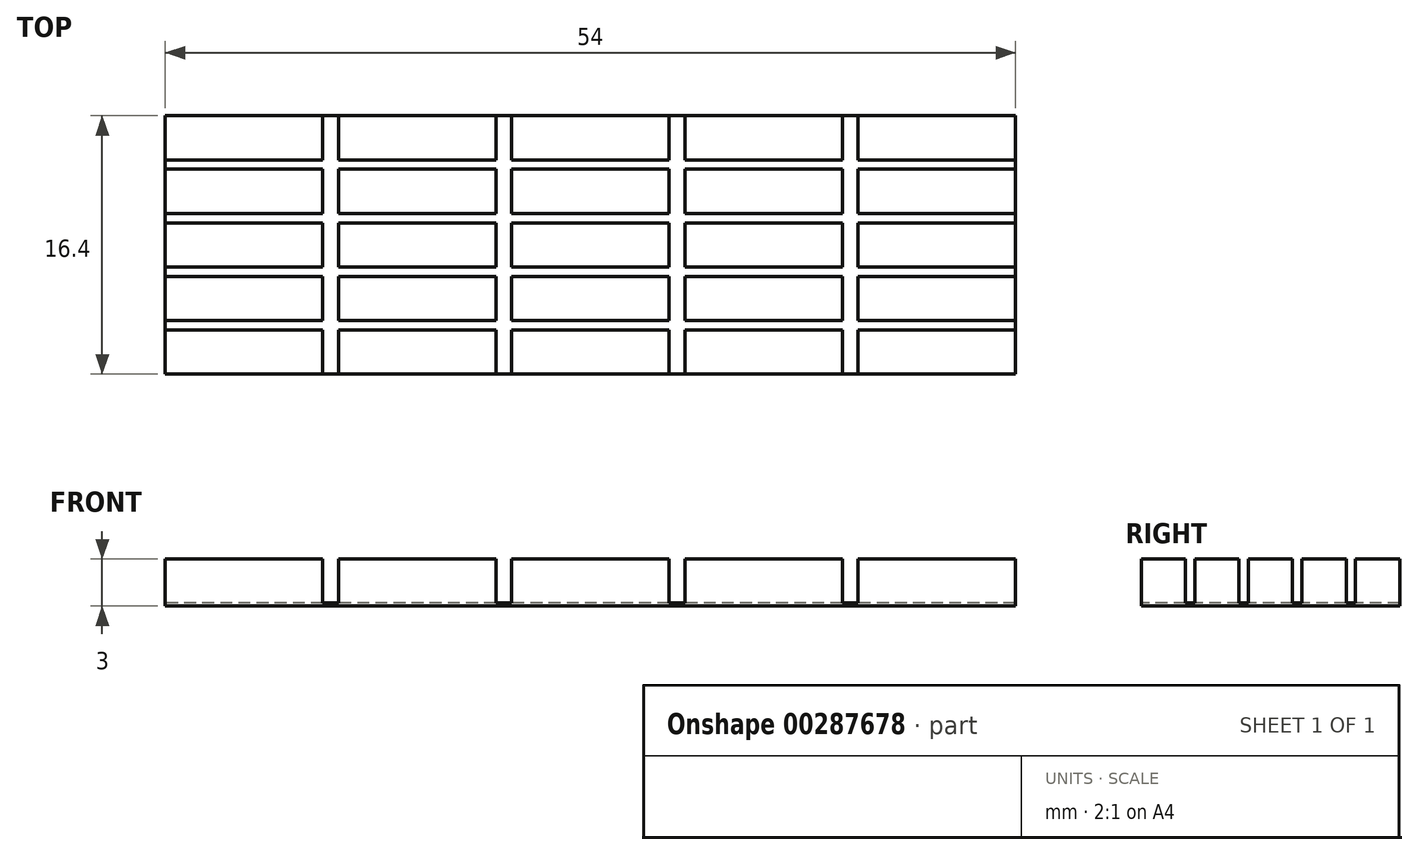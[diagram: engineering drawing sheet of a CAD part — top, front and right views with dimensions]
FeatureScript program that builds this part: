
annotation { "Feature Type Name" : "Feature", "Feature Type Description" : "" }
export const myFeature = defineFeature(function(context is Context, id is Id, definition is map)
    precondition{}
    {
        {
            var Q0;
            Q0=qCreatedBy(makeId("Top.planeOp"),FACE);
            var sketch = newSketch(context, id + "F0", { "sketchPlane" : qUnion([Q0])});
            skLineSegment(sketch, "E0", {"start": v(0, 0) * mm, "end": v(33.88, 0) * mm, "construction": true});
            skLineSegment(sketch, "E1", {"start": v(0, 0) * mm, "end": v(0, 25.36) * mm, "construction": true});
            skLineSegment(sketch, "E2.bottom", {"start": v(0, 0) * mm, "end": v(10, 0) * mm});
            skLineSegment(sketch, "E2.top", {"start": v(0, 2.8) * mm, "end": v(10, 2.8) * mm});
            skLineSegment(sketch, "E2.left", {"start": v(0, 0) * mm, "end": v(0, 2.8) * mm});
            skLineSegment(sketch, "E2.right", {"start": v(10, 0) * mm, "end": v(10, 2.8) * mm});
            skLineSegment(sketch, "E3.0.1.0", {"start": v(0, 6.2) * mm, "end": v(10, 6.2) * mm});
            skLineSegment(sketch, "E3.0.1.1", {"start": v(10, 3.4) * mm, "end": v(10, 6.2) * mm});
            skLineSegment(sketch, "E3.0.1.2", {"start": v(0, 3.4) * mm, "end": v(10, 3.4) * mm});
            skLineSegment(sketch, "E3.0.1.3", {"start": v(0, 3.4) * mm, "end": v(0, 6.2) * mm});
            skLineSegment(sketch, "E3.0.2.0", {"start": v(0, 9.6) * mm, "end": v(10, 9.6) * mm});
            skLineSegment(sketch, "E3.0.2.1", {"start": v(10, 6.8) * mm, "end": v(10, 9.6) * mm});
            skLineSegment(sketch, "E3.0.2.2", {"start": v(0, 6.8) * mm, "end": v(10, 6.8) * mm});
            skLineSegment(sketch, "E3.0.2.3", {"start": v(0, 6.8) * mm, "end": v(0, 9.6) * mm});
            skLineSegment(sketch, "E3.0.3.0", {"start": v(0, 13) * mm, "end": v(10, 13) * mm});
            skLineSegment(sketch, "E3.0.3.1", {"start": v(10, 10.2) * mm, "end": v(10, 13) * mm});
            skLineSegment(sketch, "E3.0.3.2", {"start": v(0, 10.2) * mm, "end": v(10, 10.2) * mm});
            skLineSegment(sketch, "E3.0.3.3", {"start": v(0, 10.2) * mm, "end": v(0, 13) * mm});
            skLineSegment(sketch, "E3.0.4.0", {"start": v(0, 16.4) * mm, "end": v(10, 16.4) * mm});
            skLineSegment(sketch, "E3.0.4.1", {"start": v(10, 13.6) * mm, "end": v(10, 16.4) * mm});
            skLineSegment(sketch, "E3.0.4.2", {"start": v(0, 13.6) * mm, "end": v(10, 13.6) * mm});
            skLineSegment(sketch, "E3.0.4.3", {"start": v(0, 13.6) * mm, "end": v(0, 16.4) * mm});
            skLineSegment(sketch, "E3.1.0.0", {"start": v(11, 2.8) * mm, "end": v(21, 2.8) * mm});
            skLineSegment(sketch, "E3.1.0.1", {"start": v(21, 0) * mm, "end": v(21, 2.8) * mm});
            skLineSegment(sketch, "E3.1.0.2", {"start": v(11, 0) * mm, "end": v(21, 0) * mm});
            skLineSegment(sketch, "E3.1.0.3", {"start": v(11, 0) * mm, "end": v(11, 2.8) * mm});
            skLineSegment(sketch, "E3.1.1.0", {"start": v(11, 6.2) * mm, "end": v(21, 6.2) * mm});
            skLineSegment(sketch, "E3.1.1.1", {"start": v(21, 3.4) * mm, "end": v(21, 6.2) * mm});
            skLineSegment(sketch, "E3.1.1.2", {"start": v(11, 3.4) * mm, "end": v(21, 3.4) * mm});
            skLineSegment(sketch, "E3.1.1.3", {"start": v(11, 3.4) * mm, "end": v(11, 6.2) * mm});
            skLineSegment(sketch, "E3.1.2.0", {"start": v(11, 9.6) * mm, "end": v(21, 9.6) * mm});
            skLineSegment(sketch, "E3.1.2.1", {"start": v(21, 6.8) * mm, "end": v(21, 9.6) * mm});
            skLineSegment(sketch, "E3.1.2.2", {"start": v(11, 6.8) * mm, "end": v(21, 6.8) * mm});
            skLineSegment(sketch, "E3.1.2.3", {"start": v(11, 6.8) * mm, "end": v(11, 9.6) * mm});
            skLineSegment(sketch, "E3.1.3.0", {"start": v(11, 13) * mm, "end": v(21, 13) * mm});
            skLineSegment(sketch, "E3.1.3.1", {"start": v(21, 10.2) * mm, "end": v(21, 13) * mm});
            skLineSegment(sketch, "E3.1.3.2", {"start": v(11, 10.2) * mm, "end": v(21, 10.2) * mm});
            skLineSegment(sketch, "E3.1.3.3", {"start": v(11, 10.2) * mm, "end": v(11, 13) * mm});
            skLineSegment(sketch, "E3.1.4.0", {"start": v(11, 16.4) * mm, "end": v(21, 16.4) * mm});
            skLineSegment(sketch, "E3.1.4.1", {"start": v(21, 13.6) * mm, "end": v(21, 16.4) * mm});
            skLineSegment(sketch, "E3.1.4.2", {"start": v(11, 13.6) * mm, "end": v(21, 13.6) * mm});
            skLineSegment(sketch, "E3.1.4.3", {"start": v(11, 13.6) * mm, "end": v(11, 16.4) * mm});
            skLineSegment(sketch, "E3.2.0.0", {"start": v(22, 2.8) * mm, "end": v(32, 2.8) * mm});
            skLineSegment(sketch, "E3.2.0.1", {"start": v(32, 0) * mm, "end": v(32, 2.8) * mm});
            skLineSegment(sketch, "E3.2.0.2", {"start": v(22, 0) * mm, "end": v(32, 0) * mm});
            skLineSegment(sketch, "E3.2.0.3", {"start": v(22, 0) * mm, "end": v(22, 2.8) * mm});
            skLineSegment(sketch, "E3.2.1.0", {"start": v(22, 6.2) * mm, "end": v(32, 6.2) * mm});
            skLineSegment(sketch, "E3.2.1.1", {"start": v(32, 3.4) * mm, "end": v(32, 6.2) * mm});
            skLineSegment(sketch, "E3.2.1.2", {"start": v(22, 3.4) * mm, "end": v(32, 3.4) * mm});
            skLineSegment(sketch, "E3.2.1.3", {"start": v(22, 3.4) * mm, "end": v(22, 6.2) * mm});
            skLineSegment(sketch, "E3.2.2.0", {"start": v(22, 9.6) * mm, "end": v(32, 9.6) * mm});
            skLineSegment(sketch, "E3.2.2.1", {"start": v(32, 6.8) * mm, "end": v(32, 9.6) * mm});
            skLineSegment(sketch, "E3.2.2.2", {"start": v(22, 6.8) * mm, "end": v(32, 6.8) * mm});
            skLineSegment(sketch, "E3.2.2.3", {"start": v(22, 6.8) * mm, "end": v(22, 9.6) * mm});
            skLineSegment(sketch, "E3.2.3.0", {"start": v(22, 13) * mm, "end": v(32, 13) * mm});
            skLineSegment(sketch, "E3.2.3.1", {"start": v(32, 10.2) * mm, "end": v(32, 13) * mm});
            skLineSegment(sketch, "E3.2.3.2", {"start": v(22, 10.2) * mm, "end": v(32, 10.2) * mm});
            skLineSegment(sketch, "E3.2.3.3", {"start": v(22, 10.2) * mm, "end": v(22, 13) * mm});
            skLineSegment(sketch, "E3.2.4.0", {"start": v(22, 16.4) * mm, "end": v(32, 16.4) * mm});
            skLineSegment(sketch, "E3.2.4.1", {"start": v(32, 13.6) * mm, "end": v(32, 16.4) * mm});
            skLineSegment(sketch, "E3.2.4.2", {"start": v(22, 13.6) * mm, "end": v(32, 13.6) * mm});
            skLineSegment(sketch, "E3.2.4.3", {"start": v(22, 13.6) * mm, "end": v(22, 16.4) * mm});
            skLineSegment(sketch, "E3.3.0.0", {"start": v(33, 2.8) * mm, "end": v(43, 2.8) * mm});
            skLineSegment(sketch, "E3.3.0.1", {"start": v(43, 0) * mm, "end": v(43, 2.8) * mm});
            skLineSegment(sketch, "E3.3.0.2", {"start": v(33, 0) * mm, "end": v(43, 0) * mm});
            skLineSegment(sketch, "E3.3.0.3", {"start": v(33, 0) * mm, "end": v(33, 2.8) * mm});
            skLineSegment(sketch, "E3.3.1.0", {"start": v(33, 6.2) * mm, "end": v(43, 6.2) * mm});
            skLineSegment(sketch, "E3.3.1.1", {"start": v(43, 3.4) * mm, "end": v(43, 6.2) * mm});
            skLineSegment(sketch, "E3.3.1.2", {"start": v(33, 3.4) * mm, "end": v(43, 3.4) * mm});
            skLineSegment(sketch, "E3.3.1.3", {"start": v(33, 3.4) * mm, "end": v(33, 6.2) * mm});
            skLineSegment(sketch, "E3.3.2.0", {"start": v(33, 9.6) * mm, "end": v(43, 9.6) * mm});
            skLineSegment(sketch, "E3.3.2.1", {"start": v(43, 6.8) * mm, "end": v(43, 9.6) * mm});
            skLineSegment(sketch, "E3.3.2.2", {"start": v(33, 6.8) * mm, "end": v(43, 6.8) * mm});
            skLineSegment(sketch, "E3.3.2.3", {"start": v(33, 6.8) * mm, "end": v(33, 9.6) * mm});
            skLineSegment(sketch, "E3.3.3.0", {"start": v(33, 13) * mm, "end": v(43, 13) * mm});
            skLineSegment(sketch, "E3.3.3.1", {"start": v(43, 10.2) * mm, "end": v(43, 13) * mm});
            skLineSegment(sketch, "E3.3.3.2", {"start": v(33, 10.2) * mm, "end": v(43, 10.2) * mm});
            skLineSegment(sketch, "E3.3.3.3", {"start": v(33, 10.2) * mm, "end": v(33, 13) * mm});
            skLineSegment(sketch, "E3.3.4.0", {"start": v(33, 16.4) * mm, "end": v(43, 16.4) * mm});
            skLineSegment(sketch, "E3.3.4.1", {"start": v(43, 13.6) * mm, "end": v(43, 16.4) * mm});
            skLineSegment(sketch, "E3.3.4.2", {"start": v(33, 13.6) * mm, "end": v(43, 13.6) * mm});
            skLineSegment(sketch, "E3.3.4.3", {"start": v(33, 13.6) * mm, "end": v(33, 16.4) * mm});
            skLineSegment(sketch, "E3.4.0.0", {"start": v(44, 2.8) * mm, "end": v(54, 2.8) * mm});
            skLineSegment(sketch, "E3.4.0.1", {"start": v(54, 0) * mm, "end": v(54, 2.8) * mm});
            skLineSegment(sketch, "E3.4.0.2", {"start": v(44, 0) * mm, "end": v(54, 0) * mm});
            skLineSegment(sketch, "E3.4.0.3", {"start": v(44, 0) * mm, "end": v(44, 2.8) * mm});
            skLineSegment(sketch, "E3.4.1.0", {"start": v(44, 6.2) * mm, "end": v(54, 6.2) * mm});
            skLineSegment(sketch, "E3.4.1.1", {"start": v(54, 3.4) * mm, "end": v(54, 6.2) * mm});
            skLineSegment(sketch, "E3.4.1.2", {"start": v(44, 3.4) * mm, "end": v(54, 3.4) * mm});
            skLineSegment(sketch, "E3.4.1.3", {"start": v(44, 3.4) * mm, "end": v(44, 6.2) * mm});
            skLineSegment(sketch, "E3.4.2.0", {"start": v(44, 9.6) * mm, "end": v(54, 9.6) * mm});
            skLineSegment(sketch, "E3.4.2.1", {"start": v(54, 6.8) * mm, "end": v(54, 9.6) * mm});
            skLineSegment(sketch, "E3.4.2.2", {"start": v(44, 6.8) * mm, "end": v(54, 6.8) * mm});
            skLineSegment(sketch, "E3.4.2.3", {"start": v(44, 6.8) * mm, "end": v(44, 9.6) * mm});
            skLineSegment(sketch, "E3.4.3.0", {"start": v(44, 13) * mm, "end": v(54, 13) * mm});
            skLineSegment(sketch, "E3.4.3.1", {"start": v(54, 10.2) * mm, "end": v(54, 13) * mm});
            skLineSegment(sketch, "E3.4.3.2", {"start": v(44, 10.2) * mm, "end": v(54, 10.2) * mm});
            skLineSegment(sketch, "E3.4.3.3", {"start": v(44, 10.2) * mm, "end": v(44, 13) * mm});
            skLineSegment(sketch, "E3.4.4.0", {"start": v(44, 16.4) * mm, "end": v(54, 16.4) * mm});
            skLineSegment(sketch, "E3.4.4.1", {"start": v(54, 13.6) * mm, "end": v(54, 16.4) * mm});
            skLineSegment(sketch, "E3.4.4.2", {"start": v(44, 13.6) * mm, "end": v(54, 13.6) * mm});
            skLineSegment(sketch, "E3.4.4.3", {"start": v(44, 13.6) * mm, "end": v(44, 16.4) * mm});
            skLineSegment(sketch, "E3.direction1", {"start": v(0, 2.8) * mm, "end": v(11, 2.8) * mm, "construction": true});
            skLineSegment(sketch, "E3.direction2", {"start": v(0, 2.8) * mm, "end": v(0, 6.2) * mm, "construction": true});
            skSolve(sketch);
        }
        {
            var Q0;
            Q0=qCreatedBy(makeId("Top.planeOp"),FACE);
            var sketch = newSketch(context, id + "F1", { "sketchPlane" : qUnion([Q0])});
            skLineSegment(sketch, "E4.bottom", {"start": v(0, 0) * mm, "end": v(54, 0) * mm});
            skLineSegment(sketch, "E4.top", {"start": v(0, 16.4) * mm, "end": v(54, 16.4) * mm});
            skLineSegment(sketch, "E4.left", {"start": v(0, 0) * mm, "end": v(0, 16.4) * mm});
            skLineSegment(sketch, "E4.right", {"start": v(54, 0) * mm, "end": v(54, 16.4) * mm});
            skSolve(sketch);
        }
        {
            var Q0;
            Q0 = qSketchRegion(id + "F1", true);
            extrude(context, id + "F2", {"entities" : qUnion([Q0]), "depth" : .2 * mm});
        }
        {
            var Q0;
            Q0 = qSketchRegion(id + "F0", true);
            extrude(context, id + "F3", {"entities" : qUnion([Q0]), "operationType" : NewBodyOperationType.ADD, "depth" : 3 * mm});
        }
    });
